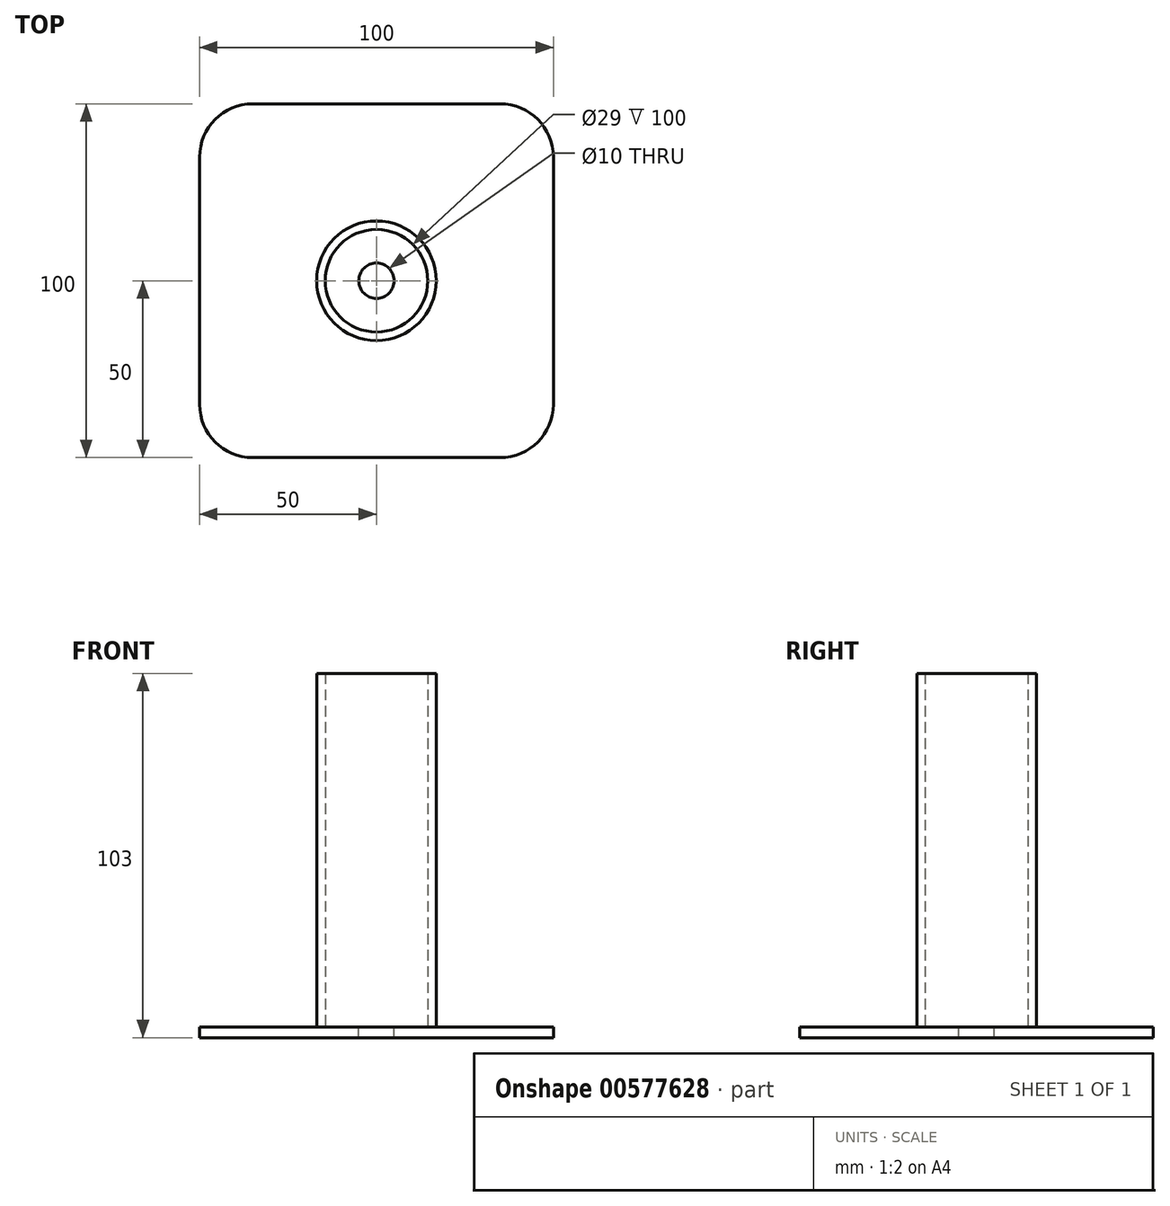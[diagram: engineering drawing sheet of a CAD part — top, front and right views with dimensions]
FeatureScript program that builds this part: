
annotation { "Feature Type Name" : "Feature", "Feature Type Description" : "" }
export const myFeature = defineFeature(function(context is Context, id is Id, definition is map)
    precondition{}
    {
        {
            var Q0;
            Q0=qCreatedBy(makeId("Top.planeOp"),FACE);
            var sketch = newSketch(context, id + "F0", { "sketchPlane" : qUnion([Q0])});
            skLineSegment(sketch, "E0.bottom", {"start": v(50, 50) * mm, "end": v(-50, 50) * mm});
            skLineSegment(sketch, "E0.top", {"start": v(50, -50) * mm, "end": v(-50, -50) * mm});
            skLineSegment(sketch, "E0.left", {"start": v(50, 50) * mm, "end": v(50, -50) * mm});
            skLineSegment(sketch, "E0.right", {"start": v(-50, 50) * mm, "end": v(-50, -50) * mm});
            skPoint(sketch, "E0.middle", {"position": v(0, 0) * mm});
            skSolve(sketch);
        }
        {
            var Q0;
            Q0=makeQuery(id+"F0.imprint","IMPRINT",FACE,{"disambiguationData":[TD([[makeQuery(id+"F0.imprint","IMPRINT",EDGE,{"derivedFrom":sQuery(id+"F0.wireOp",EDGE,"E0.bottom")}),1.0]])]});
            extrude(context, id + "F1", {"entities" : qUnion([Q0]), "depth" : 3 * mm, "offsetDistance" : 25 * mm});
        }
        {
            var Q0;
            Q0=makeQuery(id+"F1.opExtrude","CAP_FACE",FACE,{"disambiguationData":[OSD([sQuery(id+"F0.wireOp",EDGE,"E0.bottom"),sQuery(id+"F0.wireOp",EDGE,"E0.top"),sQuery(id+"F0.wireOp",EDGE,"E0.left"),sQuery(id+"F0.wireOp",EDGE,"E0.right")])],"isStart":false});
            var sketch = newSketch(context, id + "F2", { "sketchPlane" : qUnion([Q0])});
            skCircle(sketch, "E1", {"center": v(0, 0) * mm, "radius": 16.9 * mm});
            skCircle(sketch, "E2", {"center": v(0, 0) * mm, "radius": 14.5 * mm});
            skSolve(sketch);
        }
        {
            var Q0;
            Q0=makeQuery(id+"F2.imprint","IMPRINT",FACE,{"disambiguationData":[TD([[makeQuery(id+"F2.imprint","IMPRINT",EDGE,{"derivedFrom":sQuery(id+"F2.wireOp",EDGE,"E1")}),1.0]])]});
            extrude(context, id + "F3", {"entities" : qUnion([Q0]), "operationType" : NewBodyOperationType.ADD, "depth" : 100 * mm, "offsetDistance" : 25 * mm});
        }
        {
            var Q0;
            Q0=makeQuery(id+"F3.opExtrude","CAP_EDGE",EDGE,{"disambiguationData":[OSD([sQuery(id+"F2.wireOp",EDGE,"E1")])],"isStart":true});
            var Q1;
            Q1=makeQuery(id+"F1.opExtrude","SWEPT_EDGE",EDGE,{"disambiguationData":[OSD([sQuery(id+"F0.wireOp",EDGE,"E0.top"),sQuery(id+"F0.wireOp",EDGE,"E0.left")])]});
            var Q2;
            Q2=makeQuery(id+"F1.opExtrude","SWEPT_EDGE",EDGE,{"disambiguationData":[OSD([sQuery(id+"F0.wireOp",EDGE,"E0.bottom"),sQuery(id+"F0.wireOp",EDGE,"E0.left")])]});
            var Q3;
            Q3=makeQuery(id+"F1.opExtrude","SWEPT_EDGE",EDGE,{"disambiguationData":[OSD([sQuery(id+"F0.wireOp",EDGE,"E0.bottom"),sQuery(id+"F0.wireOp",EDGE,"E0.right")])]});
            var Q4;
            Q4=makeQuery(id+"F1.opExtrude","SWEPT_EDGE",EDGE,{"disambiguationData":[OSD([sQuery(id+"F0.wireOp",EDGE,"E0.top"),sQuery(id+"F0.wireOp",EDGE,"E0.right")])]});
            fillet(context, id + "F4", {"entities" : qUnion([Q0, Q1, Q2, Q3, Q4]), "radius" : 15 * mm, "allowEdgeOverflow" : false});
        }
        {
            var Q0;
            Q0=makeQuery(id+"F3.boolean.opBoolean","SPLIT",FACE,{"disambiguationData":[TD([makeQuery(id+"F3.opExtrude","SWEPT_FACE",FACE,{"disambiguationData":[OSD([sQuery(id+"F2.wireOp",EDGE,"E2")])]})])],"derivedFrom":makeQuery(id+"F1.opExtrude","CAP_FACE",FACE,{"disambiguationData":[OSD([sQuery(id+"F0.wireOp",EDGE,"E0.bottom"),sQuery(id+"F0.wireOp",EDGE,"E0.top"),sQuery(id+"F0.wireOp",EDGE,"E0.left"),sQuery(id+"F0.wireOp",EDGE,"E0.right")])],"isStart":false})});
            var sketch = newSketch(context, id + "F5", { "sketchPlane" : qUnion([Q0])});
            skCircle(sketch, "E3", {"center": v(0, 0) * mm, "radius": 5 * mm});
            skSolve(sketch);
        }
        {
            var Q0;
            Q0=makeQuery(id+"F5.imprint","IMPRINT",FACE,{"disambiguationData":[TD([[makeQuery(id+"F5.imprint","IMPRINT",EDGE,{"derivedFrom":sQuery(id+"F5.wireOp",EDGE,"E3")}),1.0]])]});
            extrude(context, id + "F6", {"entities" : qUnion([Q0]), "operationType" : NewBodyOperationType.REMOVE, "oppositeDirection" : true, "depth" : 25 * mm, "offsetDistance" : 25 * mm});
        }
    });
